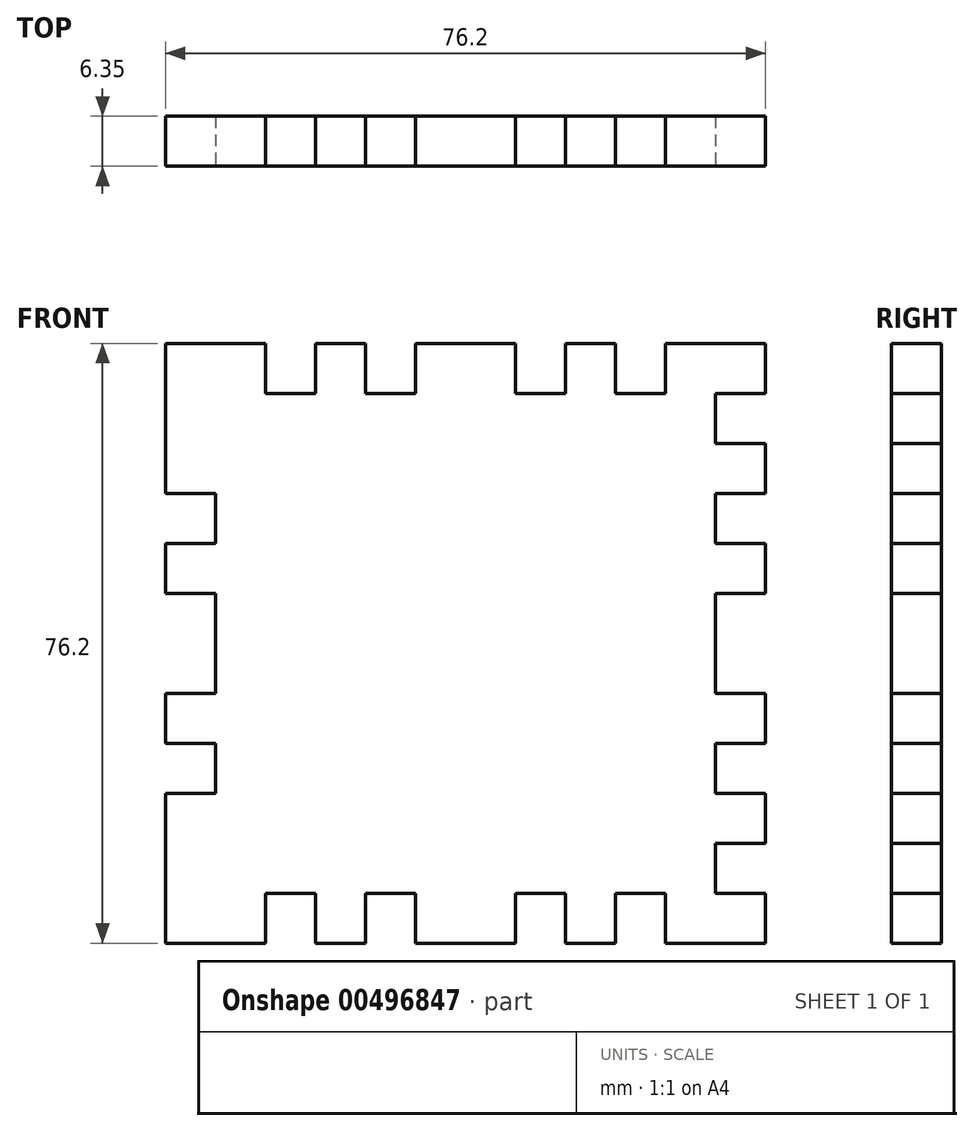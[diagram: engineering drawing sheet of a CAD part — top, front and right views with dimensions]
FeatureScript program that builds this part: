
annotation { "Feature Type Name" : "Feature", "Feature Type Description" : "" }
export const myFeature = defineFeature(function(context is Context, id is Id, definition is map)
    precondition{}
    {
        {
            var Q0;
            Q0=qCreatedBy(makeId("Front.planeOp"),FACE);
            var sketch = newSketch(context, id + "F0", { "sketchPlane" : qUnion([Q0])});
            skLineSegment(sketch, "E0.bottom", {"start": v(38.1, 38.1) * mm, "end": v(-38.1, 38.1) * mm});
            skLineSegment(sketch, "E0.top", {"start": v(38.1, -38.1) * mm, "end": v(-38.1, -38.1) * mm});
            skLineSegment(sketch, "E0.left", {"start": v(38.1, 38.1) * mm, "end": v(38.1, -38.1) * mm});
            skLineSegment(sketch, "E0.right", {"start": v(-38.1, 38.1) * mm, "end": v(-38.1, -38.1) * mm});
            skPoint(sketch, "E0.middle", {"position": v(0, 0) * mm});
            skSolve(sketch);
        }
        {
            var Q0;
            Q0=qSketchRegion(id+"F0",true);
            extrude(context, id + "F1", {"entities" : qUnion([Q0]), "depth" : 6.35 * mm});
        }
        {
            var Q0;
            Q0=makeQuery(id+"F1.opExtrude","CAP_FACE",FACE,{"disambiguationData":[OSD([sQuery(id+"F0.wireOp",EDGE,"E0.bottom"),sQuery(id+"F0.wireOp",EDGE,"E0.top"),sQuery(id+"F0.wireOp",EDGE,"E0.left"),sQuery(id+"F0.wireOp",EDGE,"E0.right")])],"isStart":false});
            var sketch = newSketch(context, id + "F2", { "sketchPlane" : qUnion([Q0])});
            skLineSegment(sketch, "E1.bottom", {"start": v(-38.1, 38.1) * mm, "end": v(-31.75, 38.1) * mm});
            skLineSegment(sketch, "E1.top", {"start": v(-38.1, 31.75) * mm, "end": v(-31.75, 31.75) * mm});
            skLineSegment(sketch, "E1.left", {"start": v(-38.1, 38.1) * mm, "end": v(-38.1, 31.75) * mm});
            skLineSegment(sketch, "E1.right", {"start": v(-31.75, 38.1) * mm, "end": v(-31.75, 31.75) * mm});
            skLineSegment(sketch, "E2.bottom", {"start": v(-31.75, 31.75) * mm, "end": v(-25.4, 31.75) * mm});
            skLineSegment(sketch, "E2.top", {"start": v(-31.75, 38.1) * mm, "end": v(-25.4, 38.1) * mm});
            skLineSegment(sketch, "E2.left", {"start": v(-31.75, 31.75) * mm, "end": v(-31.75, 38.1) * mm});
            skLineSegment(sketch, "E2.right", {"start": v(-25.4, 31.75) * mm, "end": v(-25.4, 38.1) * mm});
            skLineSegment(sketch, "E3.bottom", {"start": v(-25.4, 31.75) * mm, "end": v(-19.05, 31.75) * mm});
            skLineSegment(sketch, "E3.top", {"start": v(-25.4, 38.1) * mm, "end": v(-19.05, 38.1) * mm});
            skLineSegment(sketch, "E3.right", {"start": v(-19.05, 31.75) * mm, "end": v(-19.05, 38.1) * mm});
            skPoint(sketch, "E4.oppositeSnap0", {"position": v(-22.23, 31.75) * mm});
            skLineSegment(sketch, "E4.bottom", {"start": v(-19.05, 38.1) * mm, "end": v(-12.7, 38.1) * mm});
            skLineSegment(sketch, "E4.top", {"start": v(-19.05, 31.75) * mm, "end": v(-12.7, 31.75) * mm});
            skLineSegment(sketch, "E4.left", {"start": v(-19.05, 38.1) * mm, "end": v(-19.05, 31.75) * mm});
            skLineSegment(sketch, "E4.right", {"start": v(-12.7, 38.1) * mm, "end": v(-12.7, 31.75) * mm});
            skLineSegment(sketch, "E5.bottom", {"start": v(-12.7, 31.75) * mm, "end": v(-6.35, 31.75) * mm});
            skLineSegment(sketch, "E5.top", {"start": v(-12.7, 38.1) * mm, "end": v(-6.35, 38.1) * mm});
            skLineSegment(sketch, "E5.left", {"start": v(-12.7, 31.75) * mm, "end": v(-12.7, 38.1) * mm});
            skLineSegment(sketch, "E5.right", {"start": v(-6.35, 31.75) * mm, "end": v(-6.35, 38.1) * mm});
            skLineSegment(sketch, "E6.bottom", {"start": v(-6.35, 31.75) * mm, "end": v(0, 31.75) * mm});
            skLineSegment(sketch, "E6.top", {"start": v(-6.35, 38.1) * mm, "end": v(0, 38.1) * mm});
            skLineSegment(sketch, "E6.right", {"start": v(0, 31.75) * mm, "end": v(0, 38.1) * mm});
            skLineSegment(sketch, "E7.bottom", {"start": v(0, 31.75) * mm, "end": v(6.35, 31.75) * mm});
            skLineSegment(sketch, "E7.top", {"start": v(0, 38.1) * mm, "end": v(6.35, 38.1) * mm});
            skLineSegment(sketch, "E7.right", {"start": v(6.35, 31.75) * mm, "end": v(6.35, 38.1) * mm});
            skLineSegment(sketch, "E8.bottom", {"start": v(6.35, 31.75) * mm, "end": v(12.7, 31.75) * mm});
            skLineSegment(sketch, "E8.top", {"start": v(6.35, 38.1) * mm, "end": v(12.7, 38.1) * mm});
            skLineSegment(sketch, "E8.right", {"start": v(12.7, 31.75) * mm, "end": v(12.7, 38.1) * mm});
            skLineSegment(sketch, "E9.bottom", {"start": v(12.7, 31.75) * mm, "end": v(19.05, 31.75) * mm});
            skLineSegment(sketch, "E9.top", {"start": v(12.7, 38.1) * mm, "end": v(19.05, 38.1) * mm});
            skLineSegment(sketch, "E9.right", {"start": v(19.05, 31.75) * mm, "end": v(19.05, 38.1) * mm});
            skLineSegment(sketch, "E10.bottom", {"start": v(19.05, 31.75) * mm, "end": v(25.4, 31.75) * mm});
            skLineSegment(sketch, "E10.top", {"start": v(19.05, 38.1) * mm, "end": v(25.4, 38.1) * mm});
            skLineSegment(sketch, "E10.right", {"start": v(25.4, 31.75) * mm, "end": v(25.4, 38.1) * mm});
            skLineSegment(sketch, "E11.bottom", {"start": v(25.4, 31.75) * mm, "end": v(31.75, 31.75) * mm});
            skLineSegment(sketch, "E11.top", {"start": v(25.4, 38.1) * mm, "end": v(31.75, 38.1) * mm});
            skLineSegment(sketch, "E11.right", {"start": v(31.75, 31.75) * mm, "end": v(31.75, 38.1) * mm});
            skLineSegment(sketch, "E12.bottom", {"start": v(31.75, 31.75) * mm, "end": v(38.1, 31.75) * mm});
            skLineSegment(sketch, "E12.top", {"start": v(31.75, 38.1) * mm, "end": v(38.1, 38.1) * mm});
            skLineSegment(sketch, "E12.right", {"start": v(38.1, 31.75) * mm, "end": v(38.1, 38.1) * mm});
            skSolve(sketch);
        }
        {
            var Q0;
            Q0=makeQuery(id+"F2.imprint","IMPRINT",FACE,{"disambiguationData":[TD([[makeQuery(id+"F2.imprint","IMPRINT",EDGE,{"derivedFrom":sQuery(id+"F2.wireOp",EDGE,"E3.bottom")}),1.0]])]});
            var Q1;
            Q1=makeQuery(id+"F2.imprint","IMPRINT",FACE,{"disambiguationData":[TD([[makeQuery(id+"F2.imprint","IMPRINT",EDGE,{"derivedFrom":sQuery(id+"F2.wireOp",EDGE,"E5.bottom")}),1.0]])]});
            var Q2;
            Q2=makeQuery(id+"F2.imprint","IMPRINT",FACE,{"disambiguationData":[TD([[makeQuery(id+"F2.imprint","IMPRINT",EDGE,{"derivedFrom":sQuery(id+"F2.wireOp",EDGE,"E8.bottom")}),1.0]])]});
            var Q3;
            Q3=makeQuery(id+"F2.imprint","IMPRINT",FACE,{"disambiguationData":[TD([[makeQuery(id+"F2.imprint","IMPRINT",EDGE,{"derivedFrom":sQuery(id+"F2.wireOp",EDGE,"E10.bottom")}),1.0]])]});
            extrude(context, id + "F3", {"entities" : qUnion([Q0, Q1, Q2, Q3]), "operationType" : NewBodyOperationType.REMOVE, "endBound" : BoundingType.THROUGH_ALL, "oppositeDirection" : true, "depth" : 25.4 * mm});
        }
        {
            var Q0;
            Q0=makeQuery(id+"F1.opExtrude","CAP_FACE",FACE,{"disambiguationData":[OSD([sQuery(id+"F0.wireOp",EDGE,"E0.bottom"),sQuery(id+"F0.wireOp",EDGE,"E0.top"),sQuery(id+"F0.wireOp",EDGE,"E0.left"),sQuery(id+"F0.wireOp",EDGE,"E0.right")])],"isStart":false});
            var sketch = newSketch(context, id + "F4", { "sketchPlane" : qUnion([Q0])});
            skLineSegment(sketch, "E13.bottom", {"start": v(-38.1, -38.1) * mm, "end": v(-25.4, -38.1) * mm});
            skLineSegment(sketch, "E13.top", {"start": v(-38.1, -31.75) * mm, "end": v(-25.4, -31.75) * mm});
            skLineSegment(sketch, "E13.left", {"start": v(-38.1, -38.1) * mm, "end": v(-38.1, -31.75) * mm});
            skLineSegment(sketch, "E13.right", {"start": v(-25.4, -38.1) * mm, "end": v(-25.4, -31.75) * mm});
            skLineSegment(sketch, "E14.bottom", {"start": v(-25.4, -31.75) * mm, "end": v(-19.05, -31.75) * mm});
            skLineSegment(sketch, "E14.top", {"start": v(-25.4, -38.1) * mm, "end": v(-19.05, -38.1) * mm});
            skLineSegment(sketch, "E14.left", {"start": v(-25.4, -31.75) * mm, "end": v(-25.4, -38.1) * mm});
            skLineSegment(sketch, "E14.right", {"start": v(-19.05, -31.75) * mm, "end": v(-19.05, -38.1) * mm});
            skLineSegment(sketch, "E15.bottom", {"start": v(-19.05, -31.75) * mm, "end": v(-12.7, -31.75) * mm});
            skLineSegment(sketch, "E15.top", {"start": v(-19.05, -38.1) * mm, "end": v(-12.7, -38.1) * mm});
            skLineSegment(sketch, "E15.right", {"start": v(-12.7, -31.75) * mm, "end": v(-12.7, -38.1) * mm});
            skLineSegment(sketch, "E16.bottom", {"start": v(-12.7, -31.75) * mm, "end": v(-6.35, -31.75) * mm});
            skLineSegment(sketch, "E16.top", {"start": v(-12.7, -38.1) * mm, "end": v(-6.35, -38.1) * mm});
            skLineSegment(sketch, "E16.right", {"start": v(-6.35, -31.75) * mm, "end": v(-6.35, -38.1) * mm});
            skLineSegment(sketch, "E17.bottom", {"start": v(-6.35, -31.75) * mm, "end": v(6.35, -31.75) * mm});
            skLineSegment(sketch, "E17.top", {"start": v(-6.35, -38.1) * mm, "end": v(6.35, -38.1) * mm});
            skLineSegment(sketch, "E17.right", {"start": v(6.35, -31.75) * mm, "end": v(6.35, -38.1) * mm});
            skLineSegment(sketch, "E18.bottom", {"start": v(6.35, -31.75) * mm, "end": v(12.7, -31.75) * mm});
            skLineSegment(sketch, "E18.top", {"start": v(6.35, -38.1) * mm, "end": v(12.7, -38.1) * mm});
            skLineSegment(sketch, "E18.right", {"start": v(12.7, -31.75) * mm, "end": v(12.7, -38.1) * mm});
            skLineSegment(sketch, "E19.bottom", {"start": v(12.7, -31.75) * mm, "end": v(19.05, -31.75) * mm});
            skLineSegment(sketch, "E19.top", {"start": v(12.7, -38.1) * mm, "end": v(19.05, -38.1) * mm});
            skLineSegment(sketch, "E19.right", {"start": v(19.05, -31.75) * mm, "end": v(19.05, -38.1) * mm});
            skLineSegment(sketch, "E20.bottom", {"start": v(19.05, -31.75) * mm, "end": v(25.4, -31.75) * mm});
            skLineSegment(sketch, "E20.top", {"start": v(19.05, -38.1) * mm, "end": v(25.4, -38.1) * mm});
            skLineSegment(sketch, "E20.right", {"start": v(25.4, -31.75) * mm, "end": v(25.4, -38.1) * mm});
            skLineSegment(sketch, "E21.bottom", {"start": v(25.4, -31.75) * mm, "end": v(38.1, -31.75) * mm});
            skLineSegment(sketch, "E21.top", {"start": v(25.4, -38.1) * mm, "end": v(38.1, -38.1) * mm});
            skLineSegment(sketch, "E21.right", {"start": v(38.1, -31.75) * mm, "end": v(38.1, -38.1) * mm});
            skSolve(sketch);
        }
        {
            var Q0;
            Q0=makeQuery(id+"F4.imprint","IMPRINT",FACE,{"disambiguationData":[TD([[makeQuery(id+"F4.imprint","IMPRINT",EDGE,{"derivedFrom":sQuery(id+"F4.wireOp",EDGE,"E16.bottom")}),-1.0]])]});
            var Q1;
            Q1=makeQuery(id+"F4.imprint","IMPRINT",FACE,{"disambiguationData":[TD([[makeQuery(id+"F4.imprint","IMPRINT",EDGE,{"derivedFrom":sQuery(id+"F4.wireOp",EDGE,"E18.bottom")}),-1.0]])]});
            var Q2;
            Q2=makeQuery(id+"F4.imprint","IMPRINT",FACE,{"disambiguationData":[TD([[makeQuery(id+"F4.imprint","IMPRINT",EDGE,{"derivedFrom":sQuery(id+"F4.wireOp",EDGE,"E20.bottom")}),-1.0]])]});
            var Q3;
            Q3=makeQuery(id+"F4.imprint","IMPRINT",FACE,{"disambiguationData":[TD([[makeQuery(id+"F4.imprint","IMPRINT",EDGE,{"derivedFrom":sQuery(id+"F4.wireOp",EDGE,"E14.bottom")}),-1.0]])]});
            extrude(context, id + "F5", {"entities" : qUnion([Q0, Q1, Q2, Q3]), "operationType" : NewBodyOperationType.REMOVE, "endBound" : BoundingType.THROUGH_ALL, "oppositeDirection" : true, "depth" : 25.4 * mm});
        }
        {
            var Q0;
            Q0=makeQuery(id+"F1.opExtrude","CAP_FACE",FACE,{"disambiguationData":[OSD([sQuery(id+"F0.wireOp",EDGE,"E0.bottom"),sQuery(id+"F0.wireOp",EDGE,"E0.top"),sQuery(id+"F0.wireOp",EDGE,"E0.left"),sQuery(id+"F0.wireOp",EDGE,"E0.right")])],"isStart":false});
            var sketch = newSketch(context, id + "F6", { "sketchPlane" : qUnion([Q0])});
            skLineSegment(sketch, "E22.bottom", {"start": v(-38.1, 38.1) * mm, "end": v(-31.75, 38.1) * mm});
            skLineSegment(sketch, "E22.top", {"start": v(-38.1, 31.75) * mm, "end": v(-31.75, 31.75) * mm});
            skLineSegment(sketch, "E22.left", {"start": v(-38.1, 38.1) * mm, "end": v(-38.1, 31.75) * mm});
            skLineSegment(sketch, "E22.right", {"start": v(-31.75, 38.1) * mm, "end": v(-31.75, 31.75) * mm});
            skLineSegment(sketch, "E23.bottom", {"start": v(-31.75, 31.75) * mm, "end": v(-38.1, 31.75) * mm});
            skLineSegment(sketch, "E23.top", {"start": v(-31.75, 25.4) * mm, "end": v(-38.1, 25.4) * mm});
            skLineSegment(sketch, "E23.left", {"start": v(-31.75, 31.75) * mm, "end": v(-31.75, 25.4) * mm});
            skLineSegment(sketch, "E23.right", {"start": v(-38.1, 31.75) * mm, "end": v(-38.1, 25.4) * mm});
            skLineSegment(sketch, "E24.top", {"start": v(-31.75, 19.05) * mm, "end": v(-38.1, 19.05) * mm});
            skLineSegment(sketch, "E24.left", {"start": v(-31.75, 25.4) * mm, "end": v(-31.75, 19.05) * mm});
            skLineSegment(sketch, "E24.right", {"start": v(-38.1, 25.4) * mm, "end": v(-38.1, 19.05) * mm});
            skLineSegment(sketch, "E25.top", {"start": v(-31.75, 12.7) * mm, "end": v(-38.1, 12.7) * mm});
            skLineSegment(sketch, "E25.left", {"start": v(-31.75, 19.05) * mm, "end": v(-31.75, 12.7) * mm});
            skLineSegment(sketch, "E25.right", {"start": v(-38.1, 19.05) * mm, "end": v(-38.1, 12.7) * mm});
            skLineSegment(sketch, "E26.top", {"start": v(-31.75, 6.35) * mm, "end": v(-38.1, 6.35) * mm});
            skLineSegment(sketch, "E26.left", {"start": v(-31.75, 12.7) * mm, "end": v(-31.75, 6.35) * mm});
            skLineSegment(sketch, "E26.right", {"start": v(-38.1, 12.7) * mm, "end": v(-38.1, 6.35) * mm});
            skLineSegment(sketch, "E27.top", {"start": v(-31.75, -6.35) * mm, "end": v(-38.1, -6.35) * mm});
            skLineSegment(sketch, "E27.left", {"start": v(-31.75, 6.35) * mm, "end": v(-31.75, -6.35) * mm});
            skLineSegment(sketch, "E27.right", {"start": v(-38.1, 6.35) * mm, "end": v(-38.1, -6.35) * mm});
            skLineSegment(sketch, "E28.top", {"start": v(-31.75, -12.7) * mm, "end": v(-38.1, -12.7) * mm});
            skLineSegment(sketch, "E28.left", {"start": v(-31.75, -6.35) * mm, "end": v(-31.75, -12.7) * mm});
            skLineSegment(sketch, "E28.right", {"start": v(-38.1, -6.35) * mm, "end": v(-38.1, -12.7) * mm});
            skLineSegment(sketch, "E29.top", {"start": v(-31.75, -19.05) * mm, "end": v(-38.1, -19.05) * mm});
            skLineSegment(sketch, "E29.left", {"start": v(-31.75, -12.7) * mm, "end": v(-31.75, -19.05) * mm});
            skLineSegment(sketch, "E29.right", {"start": v(-38.1, -12.7) * mm, "end": v(-38.1, -19.05) * mm});
            skLineSegment(sketch, "E30.top", {"start": v(-31.75, -25.4) * mm, "end": v(-38.1, -25.4) * mm});
            skLineSegment(sketch, "E30.left", {"start": v(-31.75, -19.05) * mm, "end": v(-31.75, -25.4) * mm});
            skLineSegment(sketch, "E30.right", {"start": v(-38.1, -19.05) * mm, "end": v(-38.1, -25.4) * mm});
            skLineSegment(sketch, "E31.top", {"start": v(-31.75, -38.1) * mm, "end": v(-38.1, -38.1) * mm});
            skLineSegment(sketch, "E31.left", {"start": v(-31.75, -25.4) * mm, "end": v(-31.75, -38.1) * mm});
            skLineSegment(sketch, "E31.right", {"start": v(-38.1, -25.4) * mm, "end": v(-38.1, -38.1) * mm});
            skLineSegment(sketch, "E32.bottom", {"start": v(-38.1, -25.4) * mm, "end": v(-31.75, -25.4) * mm});
            skLineSegment(sketch, "E32.top", {"start": v(-38.1, -31.75) * mm, "end": v(-31.75, -31.75) * mm});
            skLineSegment(sketch, "E32.left", {"start": v(-38.1, -25.4) * mm, "end": v(-38.1, -31.75) * mm});
            skLineSegment(sketch, "E32.right", {"start": v(-31.75, -25.4) * mm, "end": v(-31.75, -31.75) * mm});
            skPoint(sketch, "E33.oppositeSnap0", {"position": v(-9.53, -31.75) * mm});
            skLineSegment(sketch, "E34.bottom", {"start": v(38.1, -38.1) * mm, "end": v(31.75, -38.1) * mm});
            skLineSegment(sketch, "E34.top", {"start": v(38.1, -31.75) * mm, "end": v(31.75, -31.75) * mm});
            skLineSegment(sketch, "E34.left", {"start": v(38.1, -38.1) * mm, "end": v(38.1, -31.75) * mm});
            skLineSegment(sketch, "E34.right", {"start": v(31.75, -38.1) * mm, "end": v(31.75, -31.75) * mm});
            skLineSegment(sketch, "E35.top", {"start": v(38.1, -25.4) * mm, "end": v(31.75, -25.4) * mm});
            skLineSegment(sketch, "E35.left", {"start": v(38.1, -31.75) * mm, "end": v(38.1, -25.4) * mm});
            skLineSegment(sketch, "E35.right", {"start": v(31.75, -31.75) * mm, "end": v(31.75, -25.4) * mm});
            skLineSegment(sketch, "E36.top", {"start": v(38.1, -19.05) * mm, "end": v(31.75, -19.05) * mm});
            skLineSegment(sketch, "E36.left", {"start": v(38.1, -25.4) * mm, "end": v(38.1, -19.05) * mm});
            skLineSegment(sketch, "E36.right", {"start": v(31.75, -25.4) * mm, "end": v(31.75, -19.05) * mm});
            skLineSegment(sketch, "E37.top", {"start": v(38.1, -12.7) * mm, "end": v(31.75, -12.7) * mm});
            skLineSegment(sketch, "E37.left", {"start": v(38.1, -19.05) * mm, "end": v(38.1, -12.7) * mm});
            skLineSegment(sketch, "E37.right", {"start": v(31.75, -19.05) * mm, "end": v(31.75, -12.7) * mm});
            skLineSegment(sketch, "E38.top", {"start": v(38.1, -6.35) * mm, "end": v(31.75, -6.35) * mm});
            skLineSegment(sketch, "E38.left", {"start": v(38.1, -12.7) * mm, "end": v(38.1, -6.35) * mm});
            skLineSegment(sketch, "E38.right", {"start": v(31.75, -12.7) * mm, "end": v(31.75, -6.35) * mm});
            skLineSegment(sketch, "E39.top", {"start": v(38.1, 0) * mm, "end": v(31.75, 0) * mm});
            skLineSegment(sketch, "E39.left", {"start": v(38.1, -6.35) * mm, "end": v(38.1, 0) * mm});
            skLineSegment(sketch, "E39.right", {"start": v(31.75, -6.35) * mm, "end": v(31.75, 0) * mm});
            skLineSegment(sketch, "E40.top", {"start": v(38.1, 6.35) * mm, "end": v(31.75, 6.35) * mm});
            skLineSegment(sketch, "E40.left", {"start": v(38.1, 0) * mm, "end": v(38.1, 6.35) * mm});
            skLineSegment(sketch, "E40.right", {"start": v(31.75, 0) * mm, "end": v(31.75, 6.35) * mm});
            skLineSegment(sketch, "E41.top", {"start": v(38.1, 12.7) * mm, "end": v(31.75, 12.7) * mm});
            skLineSegment(sketch, "E41.left", {"start": v(38.1, 6.35) * mm, "end": v(38.1, 12.7) * mm});
            skLineSegment(sketch, "E41.right", {"start": v(31.75, 6.35) * mm, "end": v(31.75, 12.7) * mm});
            skLineSegment(sketch, "E42.top", {"start": v(38.1, 19.05) * mm, "end": v(31.75, 19.05) * mm});
            skLineSegment(sketch, "E42.left", {"start": v(38.1, 12.7) * mm, "end": v(38.1, 19.05) * mm});
            skLineSegment(sketch, "E42.right", {"start": v(31.75, 12.7) * mm, "end": v(31.75, 19.05) * mm});
            skLineSegment(sketch, "E43.top", {"start": v(38.1, 25.4) * mm, "end": v(31.75, 25.4) * mm});
            skLineSegment(sketch, "E43.left", {"start": v(38.1, 19.05) * mm, "end": v(38.1, 25.4) * mm});
            skLineSegment(sketch, "E43.right", {"start": v(31.75, 19.05) * mm, "end": v(31.75, 25.4) * mm});
            skLineSegment(sketch, "E44.top", {"start": v(38.1, 31.75) * mm, "end": v(31.75, 31.75) * mm});
            skLineSegment(sketch, "E44.left", {"start": v(38.1, 25.4) * mm, "end": v(38.1, 31.75) * mm});
            skLineSegment(sketch, "E44.right", {"start": v(31.75, 25.4) * mm, "end": v(31.75, 31.75) * mm});
            skLineSegment(sketch, "E45.top", {"start": v(38.1, 38.1) * mm, "end": v(31.75, 38.1) * mm});
            skLineSegment(sketch, "E45.left", {"start": v(38.1, 31.75) * mm, "end": v(38.1, 38.1) * mm});
            skLineSegment(sketch, "E45.right", {"start": v(31.75, 31.75) * mm, "end": v(31.75, 38.1) * mm});
            skSolve(sketch);
        }
        {
            var Q0;
            {var subQ7=sQuery(id+"F6.wireOp",EDGE,"E33.left");Q0=makeQuery(id+"F6.imprint","IMPRINT",FACE,{"disambiguationData":[TD([[makeQuery(id+"F6.imprint","IMPRINT",EDGE,{"derivedFrom":subQ7}),-1.0]])]});}
            var Q1;
            Q1=makeQuery(id+"F6.imprint","IMPRINT",FACE,{"disambiguationData":[TD([[makeQuery(id+"F6.imprint","IMPRINT",EDGE,{"derivedFrom":sQuery(id+"F6.wireOp",EDGE,"E32.bottom")}),-1.0]])]});
            var Q2;
            Q2=makeQuery(id+"F6.imprint","IMPRINT",FACE,{"disambiguationData":[TD([[makeQuery(id+"F6.imprint","IMPRINT",EDGE,{"derivedFrom":sQuery(id+"F6.wireOp",EDGE,"E28.top")}),1.0]])]});
            var Q3;
            Q3=makeQuery(id+"F6.imprint","IMPRINT",FACE,{"disambiguationData":[TD([[makeQuery(id+"F6.imprint","IMPRINT",EDGE,{"derivedFrom":sQuery(id+"F6.wireOp",EDGE,"E26.top")}),1.0]])]});
            var Q4;
            Q4=makeQuery(id+"F6.imprint","IMPRINT",FACE,{"disambiguationData":[TD([[makeQuery(id+"F6.imprint","IMPRINT",EDGE,{"derivedFrom":sQuery(id+"F6.wireOp",EDGE,"E24.top")}),1.0]])]});
            var Q5;
            Q5=makeQuery(id+"F6.imprint","IMPRINT",FACE,{"disambiguationData":[TD([[makeQuery(id+"F6.imprint","IMPRINT",EDGE,{"derivedFrom":sQuery(id+"F6.wireOp",EDGE,"E23.bottom")}),1.0]])]});
            var Q6;
            {var subQ0=sQuery(id+"F6.wireOp",EDGE,"ce4bbc26-4623-4cc1-b934-9bebaf63a0d9.right");Q6=makeQuery(id+"F6.imprint","IMPRINT",FACE,{"disambiguationData":[TD([[makeQuery(id+"F6.imprint","IMPRINT",EDGE,{"derivedFrom":subQ0}),1.0]])]});}
            var Q7;
            {var subQ0=sQuery(id+"F6.wireOp",EDGE,"7441e530-7b21-4ff4-9a56-8b1e1a90f8be.right");Q7=makeQuery(id+"F6.imprint","IMPRINT",FACE,{"disambiguationData":[TD([[makeQuery(id+"F6.imprint","IMPRINT",EDGE,{"derivedFrom":subQ0}),1.0]])]});}
            var Q8;
            {var subQ0=sQuery(id+"F6.wireOp",EDGE,"a8066e9f-8eac-4923-83a9-87fd62ee7c64.right");Q8=makeQuery(id+"F6.imprint","IMPRINT",FACE,{"disambiguationData":[TD([[makeQuery(id+"F6.imprint","IMPRINT",EDGE,{"derivedFrom":subQ0}),1.0]])]});}
            var Q9;
            {var subQ0=sQuery(id+"F6.wireOp",EDGE,"4c67c5ab-1dc8-4b44-bbe4-2fddc86bda01.right");Q9=makeQuery(id+"F6.imprint","IMPRINT",FACE,{"disambiguationData":[TD([[makeQuery(id+"F6.imprint","IMPRINT",EDGE,{"derivedFrom":subQ0}),1.0]])]});}
            var Q10;
            {var subQ0=sQuery(id+"F6.wireOp",EDGE,"E33.left");Q10=makeQuery(id+"F6.imprint","IMPRINT",FACE,{"disambiguationData":[TD([[makeQuery(id+"F6.imprint","IMPRINT",EDGE,{"derivedFrom":subQ0}),1.0]])]});}
            var Q11;
            {var subQ0=sQuery(id+"F6.wireOp",EDGE,"0f048f16-57cd-401f-9e50-952359310382.left");Q11=makeQuery(id+"F6.imprint","IMPRINT",FACE,{"disambiguationData":[TD([[makeQuery(id+"F6.imprint","IMPRINT",EDGE,{"derivedFrom":subQ0}),1.0]])]});}
            var Q12;
            Q12=makeQuery(id+"F6.imprint","IMPRINT",FACE,{"disambiguationData":[TD([[makeQuery(id+"F6.imprint","IMPRINT",EDGE,{"derivedFrom":sQuery(id+"F6.wireOp",EDGE,"E34.top")}),-1.0]])]});
            var Q13;
            Q13=makeQuery(id+"F6.imprint","IMPRINT",FACE,{"disambiguationData":[TD([[makeQuery(id+"F6.imprint","IMPRINT",EDGE,{"derivedFrom":sQuery(id+"F6.wireOp",EDGE,"E36.top")}),-1.0]])]});
            var Q14;
            Q14=makeQuery(id+"F6.imprint","IMPRINT",FACE,{"disambiguationData":[TD([[makeQuery(id+"F6.imprint","IMPRINT",EDGE,{"derivedFrom":sQuery(id+"F6.wireOp",EDGE,"E38.top")}),-1.0]])]});
            var Q15;
            Q15=makeQuery(id+"F6.imprint","IMPRINT",FACE,{"disambiguationData":[TD([[makeQuery(id+"F6.imprint","IMPRINT",EDGE,{"derivedFrom":sQuery(id+"F6.wireOp",EDGE,"E39.top")}),-1.0]])]});
            var Q16;
            Q16=makeQuery(id+"F6.imprint","IMPRINT",FACE,{"disambiguationData":[TD([[makeQuery(id+"F6.imprint","IMPRINT",EDGE,{"derivedFrom":sQuery(id+"F6.wireOp",EDGE,"E41.top")}),-1.0]])]});
            var Q17;
            Q17=makeQuery(id+"F6.imprint","IMPRINT",FACE,{"disambiguationData":[TD([[makeQuery(id+"F6.imprint","IMPRINT",EDGE,{"derivedFrom":sQuery(id+"F6.wireOp",EDGE,"E43.top")}),-1.0]])]});
            extrude(context, id + "F7", {"entities" : qUnion([Q0, Q1, Q2, Q3, Q4, Q5, Q6, Q7, Q8, Q9, Q10, Q11, Q12, Q13, Q14, Q15, Q16, Q17]), "operationType" : NewBodyOperationType.REMOVE, "endBound" : BoundingType.THROUGH_ALL, "oppositeDirection" : true, "depth" : 25.4 * mm});
        }
    });
